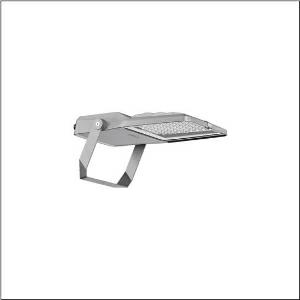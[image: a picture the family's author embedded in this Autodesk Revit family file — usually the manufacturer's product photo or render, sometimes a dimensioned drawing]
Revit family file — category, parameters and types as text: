
# Revit family: floodlight_fl_21_iq_mini___pl43_5xa7772b3a1a_8813
name_source: partatom
category: Lighting Fixtures
units: mm (PartAtom-declared; Revit-internal decimal feet)

## family parameters
Cut with Voids When Loaded = No
Host = Face
Light Source = No
Part Type = Normal
Room Calculation Point = No
Round Connector Dimension = Use Diameter
Shared = No

## types (1)
- --- (1 x LED, 5510 lm, 45.5 W, 3000K)
    Apparent Load = 46 VA
    CIE Flux Codes = 27 78 99 100 100
    Color Rendering = 80
    Color Temperature = 3000K
    Default Elevation = 1800 mm
    Description = Floodlight FL 21 iQ mini, floodlight, primary light control with lens, of PMMA, primary optical cover: protective disc, of toughened safety glass, transparent, light distribution: PL43, light emission: direct distribution, installation type: surface-mounted, lamps: LED, High Power LED, rated values: 5.510lm | 45,5W | 121,1lm/W (begin service life); end service life: 5.510lm | 48W; at 50% lumin. flux: 2.755lm | 21,4W | 128,7lm/W, colour temperature: 3000K, colour rendering: CRI > 80, light colour: 830, light setting 1 begin service life: 100% | 5.510lm | 45,5W | 121,1lm/W | 3.000K, light setting 1 end service life: 48W, further light settings possible, control: Street-Remote, Auto-Match, Temp-Guard, Night-Set, Smart-Wire, Desk-Remote (wireless, voltage-free reading and setting of iQ features in the workshop via application-optimized NFC function/RFID function), optimised constant luminous flux control (CLO 2.0), pre-setting: linear dimming characteristic, with terminal, 6-pole, mains connection: 220..240V, AC, 50/60Hz, luminaire housing, of diecast aluminium, powder-coated, SITECO metallic grey (DB 702S), corrosivity category C5 mid according to DIN EN ISO 12944suitable for swimming poolschlorine-resistant, sealing non-destructively replaceable, mounting bracket, of steel, galvanised, powder-coated, SITECO metallic grey (DB 702S), protection rating (complete): IP66, insulation class (complete): insulation class II (safety insulation), certification: CE, ENEC, VDE, protection symbol: D, impact resistance: IK08, permissible operating ambient temperature: -40..+40°C, permissible operating ambient temperature for outdoor applications: -40..+50°C, standard: DIN EN 12944, LABS conformity tested according to VDMA 24364:2018-05, packaging unit: 1 piece

Light Distribution: PL43
    Height = 70 mm
    Lamp = 1 x LED
    Lamp Light Flux = 5510 lm
    Lamp Power = 45.5 W
    Lamp count = 1
    Length = 485 mm
    Luminous efficacy = 121 lm/W
    Manufacturer = Siteco
    ModVariant = No
    Model = 5XA7772B3A1A
    Number of Poles = 1
    OnlyDefault = Yes
    Power Factor = 1
    Product Name = Floodlight FL 21 iQ mini | PL43
    Product group = floodlight | pylon annexe
    ProductGroupID = 6201
    Protection Class = Protection class II
    Protection Degree = IP 66
    RLX_Detail_Level = 1
    RLX_Emergency_Light_Flux = 0 lm
    RLX_Emergency_Type = 0
    RLX_Emergency_Type_DB = No
    RlxData = <blob elided: 96381 chars, md5=be23313e>
    Socket = socket
    Standby Power = 0 W
    System Light Flux = 5510 lm
    System Power = 46 W
    Type Comments = factory setting: luminous flux: 100 % | dim-lin: 254 | 463 mA
    Type Image = l_1006845.jpg
    URL = http://relux.com
    VarID = @adj_162215
    Voltage = 0 V
    Weight = 0.00 kg
    Width = 337 mm

## geometry (parser evidence)
native form markers: Blend x4, Sweep x11
no freeform markers — native parametric forms only
